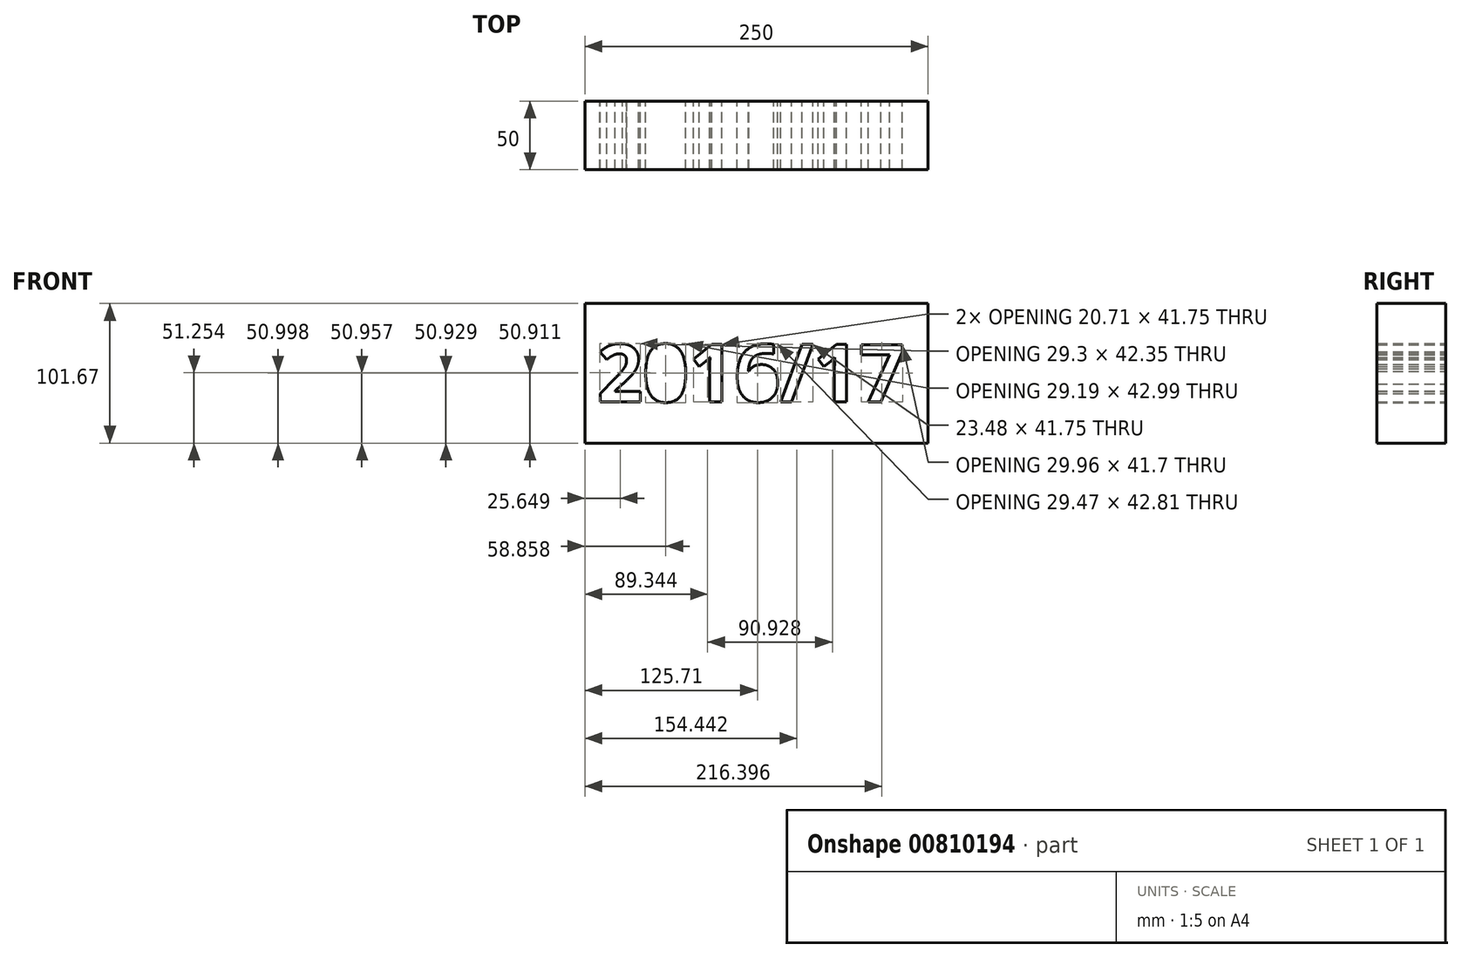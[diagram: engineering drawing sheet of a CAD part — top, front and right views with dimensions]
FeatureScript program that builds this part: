
annotation { "Feature Type Name" : "Feature", "Feature Type Description" : "" }
export const myFeature = defineFeature(function(context is Context, id is Id, definition is map)
    precondition{}
    {
        {
            var Q0;
            Q0=qCreatedBy(makeId("Front.planeOp"),FACE);
            var sketch = newSketch(context, id + "F0", { "sketchPlane" : qUnion([Q0])});
            skLineSegment(sketch, "E0.bottom", {"start": v(-119.43, 55.75) * mm, "end": v(130.57, 55.75) * mm});
            skLineSegment(sketch, "E0.top", {"start": v(-119.43, -45.92) * mm, "end": v(130.57, -45.92) * mm});
            skLineSegment(sketch, "E0.left", {"start": v(-119.43, 55.75) * mm, "end": v(-119.43, -45.92) * mm});
            skLineSegment(sketch, "E0.right", {"start": v(130.57, 55.75) * mm, "end": v(130.57, -45.92) * mm});
            skText(sketch, "E1", { "text": "2016/17", "fontName": "OpenSans-Bold.ttf"});
            const initialGuessF0  = {"E1": [-0.11066, -0.01584, 1, 0, 0.04211]};
            skSetInitialGuess(sketch, initialGuessF0);
            skSolve(sketch);
        }
        {
            var Q0;
            Q0=makeQuery(id+"F0.imprint","IMPRINT",FACE,{"disambiguationData":[TD([[makeQuery(id+"F0.imprint","IMPRINT",EDGE,{"derivedFrom":sQuery(id+"F0.wireOp",EDGE,"E0.bottom")}),-1.0]])]});
            extrude(context, id + "F1", {"entities" : qUnion([Q0]), "depth" : 50 * mm, "offsetDistance" : 25 * mm});
        }
    });
